# Revit family: AFX-Pratt-Outdoor_Sconce
name_source: partatom
category: Lighting Fixtures
units: mm (PartAtom-declared; Revit-internal decimal feet)

## family parameters
Cut with Voids When Loaded = No
Host = Face
Light Source = No
Part Type = Normal
Room Calculation Point = No
Round Connector Dimension = Use Diameter
Shared = No

## types (1)
- PRTW0905LAJENBK
    Apparent Load = 0 VA
    Arm Finish = AFX - Black Steel
    Assembly Code = D5020200
    Body Finish = AFX - Black Steel
    Colour Rendering Index = 80
    Default Elevation = 48"
    Depth = 7 1/2"
    Description = Outdoor LED Pivoting Heads To Adjust Light Direction - 9"W x 7 1/2"D x 5"H
    Diffuser Finish = AFX - White Acrylic
    Height = 5"
    Housing Finish = AFX - Black Steel
    Keynote = 12500
    Manufacturer = AFX Inc
    Model = PRTW0905LAJENBK
    Power Factor = 1
    Product Documentation Link = https://www.afxinc.com
    Revit File Built By = https://servex-us.com
    Type Comments = Pratt
    URL = https://www.afxinc.com
    Voltage = 120 V
    Wattage Comments = 9
    Width = 9"

## geometry (parser evidence)
native form markers: Sweep x8
no freeform markers — native parametric forms only
